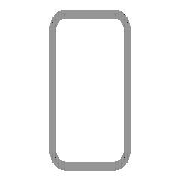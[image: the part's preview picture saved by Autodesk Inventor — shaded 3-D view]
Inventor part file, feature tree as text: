
AUTODESK INVENTOR PART (.ipt)
format: ipt  version: 2025 (Build 290162010, 162A)  size: 133,120 bytes
history: native  units: mm (DEFAULTED — no unit token found)
features: other x4, sketch x1, plane x1
ambient origin geometry x8: Origin, YZ Plane, XZ Plane, XY Plane, X Axis, Y Axis, Z Axis, Center Point
bodies: Solid1 (feature_tree), Body (feature_tree)
feature tree (6):
  parser-record x1  (decoder bookkeeping rows leaked as tree rows — omitted from the tree; the rows remain in map.json)
  other  "Driven Length"
  other  "Start Plane"
  other  "End Plane"
  sketch  "Sketch3"  dims[d3=260.0mm d4=0.0mm d7=4.0mm d9=20.0mm d11=40.0mm d12=2.0mm d13=-0.0mm d14=260.0mm d15=10.0mm d16=20.0mm d17=90.0deg d18=260.0mm]
  plane  "Work Plane3"
